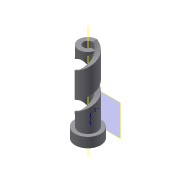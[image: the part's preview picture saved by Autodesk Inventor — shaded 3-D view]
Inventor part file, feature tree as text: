
AUTODESK INVENTOR PART (.ipt)
format: ipt  version: 2018 (Build 220112000, 112)  size: 215,552 bytes
history: native  units: mm
features: sketch x8, extrude x7, plane x1, other x1, helix x1
ambient origin geometry x8: Origin, YZ Plane, XZ Plane, XY Plane, X Axis, Y Axis, Z Axis, Center Point
bodies: Solid1 (feature_tree)
feature tree (18):
  extrude  "Extrusion1"  Depth=3.0mm
  extrude  "Extrusion2"  Depth=18.0mm
  extrude  "Extrusion3"  Depth=7.0mm
  extrude  "Extrusion5"  Depth=1.0mm
  plane  "Work Plane1"
  extrude  "Extrusion8"  Depth=6.5mm
  sketch  "Sketch9"  dims[d34=12.0mm d44=6.0mm]
  other  "Work Axis1"
  helix  "Coil2"  [1 undecoded]
  extrude  "Extrusión9"  Depth=6.0mm
  extrude  "Extrusión10"  Depth=5.0mm
  sketch  "Sketch1"  dims[d0=6.0mm d1=3.0mm]
  sketch  "Sketch2"  dims[d2=80.0mm d4=360.0deg d6=18.0mm]
  sketch  "Sketch3"  dims[d7=7.0mm d8=0.0mm d9=13.0mm]
  sketch  "Sketch5"  dims[d10=1.0mm d11=0.0mm d12=13.0mm]
  sketch  "Sketch8"  dims[d13=50.0mm d14=0.0mm d25=6.5mm d26=6.0mm d27=0.0mm]
  sketch  "Boceto13"  dims[d45=4.5mm d46=0.0mm d61=5.0mm]
  sketch  "Boceto14"  dims[d62=7.0mm d63=25.0mm d64=50.0mm d65=40.0mm d66=0.174533mm d67=90.0deg d68=90.0deg d69=0.0mm d70=0.0mm d72=7.0mm d73=0.0mm d74=2.0mm d75=0.0mm]
note: 1 required parameter value undecoded (feature->parameter linkage not recoverable at this tier; creation-order binding heuristic only, values carry confidence <= 0.55)
